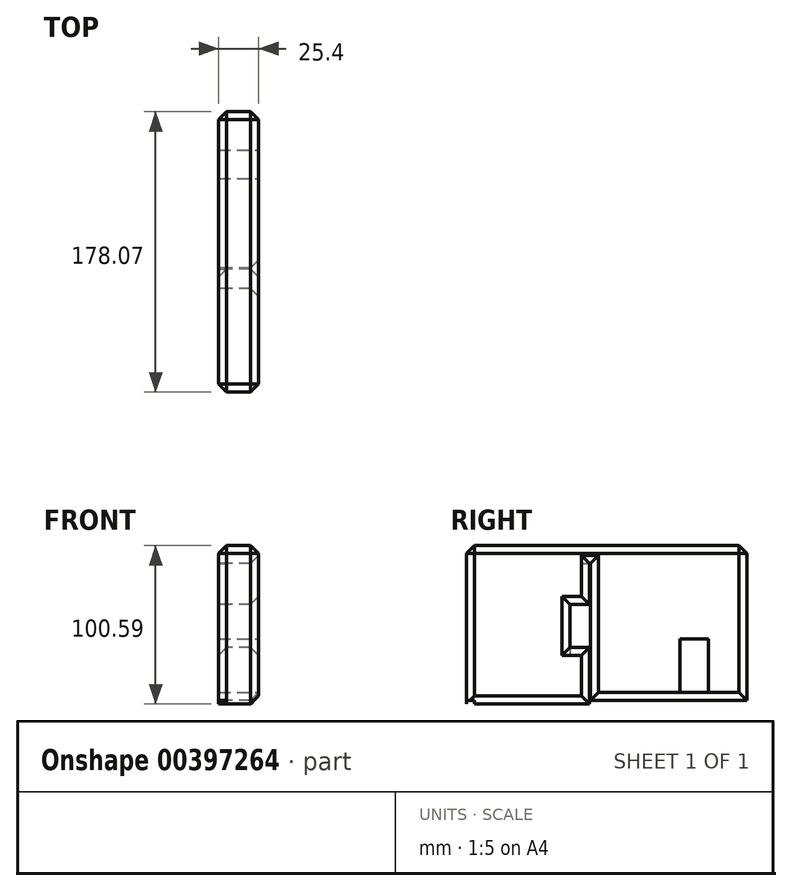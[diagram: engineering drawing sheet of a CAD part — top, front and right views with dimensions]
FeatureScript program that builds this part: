
annotation { "Feature Type Name" : "Feature", "Feature Type Description" : "" }
export const myFeature = defineFeature(function(context is Context, id is Id, definition is map)
    precondition{}
    {
        {
            var Q0;
            Q0=qCreatedBy(makeId("Right.planeOp"),FACE);
            var sketch = newSketch(context, id + "F0", { "sketchPlane" : qUnion([Q0])});
            skLineSegment(sketch, "E0.bottom", {"start": v(-42.81, -11.37) * mm, "end": v(56.46, -11.37) * mm});
            skLineSegment(sketch, "E0.top", {"start": v(-42.81, 42.16) * mm, "end": v(56.46, 42.16) * mm});
            skLineSegment(sketch, "E0.left", {"start": v(-42.81, -11.37) * mm, "end": v(-42.81, 42.16) * mm});
            skLineSegment(sketch, "E0.right", {"start": v(56.46, -11.37) * mm, "end": v(56.46, 42.16) * mm});
            skLineSegment(sketch, "E1.bottom", {"start": v(-55.84, 15.92) * mm, "end": v(-121.61, 15.92) * mm});
            skLineSegment(sketch, "E1.top", {"start": v(-55.84, -10.3) * mm, "end": v(-121.61, -10.3) * mm});
            skLineSegment(sketch, "E1.left", {"start": v(-55.84, 15.92) * mm, "end": v(-55.84, -10.3) * mm});
            skLineSegment(sketch, "E1.right", {"start": v(-121.61, 15.92) * mm, "end": v(-121.61, -10.3) * mm});
            skLineSegment(sketch, "E2.bottom", {"start": v(-121.61, 15.92) * mm, "end": v(-43.43, 15.92) * mm});
            skLineSegment(sketch, "E2.top", {"start": v(-121.61, 53.42) * mm, "end": v(-43.43, 53.42) * mm});
            skLineSegment(sketch, "E2.left", {"start": v(-121.61, 15.92) * mm, "end": v(-121.61, 53.42) * mm});
            skLineSegment(sketch, "E2.right", {"start": v(-43.43, 15.92) * mm, "end": v(-43.43, 53.42) * mm});
            skLineSegment(sketch, "E3.bottom", {"start": v(-55.84, -10.3) * mm, "end": v(-42.81, -10.3) * mm});
            skLineSegment(sketch, "E3.top", {"start": v(-55.84, -11.37) * mm, "end": v(-42.81, -11.37) * mm});
            skLineSegment(sketch, "E3.left", {"start": v(-55.84, -10.3) * mm, "end": v(-55.84, -11.37) * mm});
            skLineSegment(sketch, "E3.right", {"start": v(-42.81, -10.3) * mm, "end": v(-42.81, -11.37) * mm});
            skLineSegment(sketch, "E4.bottom", {"start": v(-42.81, -10.3) * mm, "end": v(-55.84, -10.3) * mm});
            skLineSegment(sketch, "E4.top", {"start": v(-42.81, 15.92) * mm, "end": v(-55.84, 15.92) * mm});
            skLineSegment(sketch, "E4.left", {"start": v(-42.81, -10.3) * mm, "end": v(-42.81, 15.92) * mm});
            skLineSegment(sketch, "E4.right", {"start": v(-55.84, -10.3) * mm, "end": v(-55.84, 15.92) * mm});
            skLineSegment(sketch, "E5.bottom", {"start": v(-43.43, 53.42) * mm, "end": v(56.46, 53.42) * mm});
            skLineSegment(sketch, "E5.top", {"start": v(-43.43, 42.16) * mm, "end": v(56.46, 42.16) * mm});
            skLineSegment(sketch, "E5.left", {"start": v(-43.43, 53.42) * mm, "end": v(-43.43, 42.16) * mm});
            skLineSegment(sketch, "E5.right", {"start": v(56.46, 53.42) * mm, "end": v(56.46, 42.16) * mm});
            skLineSegment(sketch, "E6.top", {"start": v(-42.81, -45.03) * mm, "end": v(56.46, -45.03) * mm});
            skLineSegment(sketch, "E6.left", {"start": v(-42.81, -11.37) * mm, "end": v(-42.81, -45.03) * mm});
            skLineSegment(sketch, "E6.right", {"start": v(56.46, -11.37) * mm, "end": v(56.46, -45.03) * mm});
            skLineSegment(sketch, "E7.bottom", {"start": v(-121.61, -10.3) * mm, "end": v(-43.43, -10.3) * mm});
            skLineSegment(sketch, "E7.top", {"start": v(-121.61, -47.17) * mm, "end": v(-43.43, -47.17) * mm});
            skLineSegment(sketch, "E7.left", {"start": v(-121.61, -10.3) * mm, "end": v(-121.61, -47.17) * mm});
            skLineSegment(sketch, "E7.right", {"start": v(-43.43, -10.3) * mm, "end": v(-43.43, -47.17) * mm});
            skSolve(sketch);
        }
        {
            var Q0;
            {var subQ1=sQuery(id+"F0.wireOp",EDGE,"E2.bottom");Q0=makeQuery(id+"F0.imprint","IMPRINT",FACE,{"disambiguationData":[TD([[makeQuery(id+"F0.imprint","IMPRINT",EDGE,{"derivedFrom":subQ1}),1.0]])]});}
            var Q1;
            {var subQ0=sQuery(id+"F0.wireOp",EDGE,"E1.right");Q1=makeQuery(id+"F0.imprint","IMPRINT",FACE,{"disambiguationData":[TD([[makeQuery(id+"F0.imprint","IMPRINT",EDGE,{"derivedFrom":subQ0}),1.0]])]});}
            var Q2;
            {var subQ4=sQuery(id+"F0.wireOp",EDGE,"E4.bottom");Q2=makeQuery(id+"F0.imprint","IMPRINT",FACE,{"disambiguationData":[TD([[makeQuery(id+"F0.imprint","IMPRINT",EDGE,{"derivedFrom":subQ4}),-1.0]])]});}
            var Q3;
            {var subQ2=sQuery(id+"F0.wireOp",EDGE,"E3.left");Q3=makeQuery(id+"F0.imprint","IMPRINT",FACE,{"disambiguationData":[TD([[makeQuery(id+"F0.imprint","IMPRINT",EDGE,{"derivedFrom":subQ2}),-1.0]])]});}
            var Q4;
            Q4=makeQuery(id+"F0.imprint","IMPRINT",FACE,{"disambiguationData":[TD([[makeQuery(id+"F0.imprint","IMPRINT",EDGE,{"derivedFrom":sQuery(id+"F0.wireOp",EDGE,"E0.bottom")}),-1.0]])]});
            var Q5;
            {var subQ1=sQuery(id+"F0.wireOp",EDGE,"E0.left");Q5=makeQuery(id+"F0.imprint","IMPRINT",FACE,{"disambiguationData":[TD([[makeQuery(id+"F0.imprint","IMPRINT",EDGE,{"derivedFrom":subQ1}),-1.0]])]});}
            var Q6;
            Q6=makeQuery(id+"F0.imprint","IMPRINT",FACE,{"disambiguationData":[TD([[makeQuery(id+"F0.imprint","IMPRINT",EDGE,{"derivedFrom":sQuery(id+"F0.wireOp",EDGE,"E5.bottom")}),-1.0]])]});
            extrude(context, id + "F1", {"entities" : qUnion([Q0, Q1, Q2, Q3, Q4, Q5, Q6]), "depth" : 25.4 * mm});
        }
        {
            var Q0;
            Q0=makeQuery(id+"F1.opExtrude","CAP_EDGE",EDGE,{"disambiguationData":[OSD([sQuery(id+"F0.wireOp",EDGE,"E2.top"),sQuery(id+"F0.wireOp",EDGE,"E5.bottom")])],"isStart":true});
            var Q1;
            Q1=makeQuery(id+"F1.opExtrude","SWEPT_FACE",FACE,{"disambiguationData":[OSD([sQuery(id+"F0.wireOp",EDGE,"E2.top"),sQuery(id+"F0.wireOp",EDGE,"E5.bottom")])]});
            var Q2;
            Q2=makeQuery(id+"F1.opExtrude","CAP_EDGE",EDGE,{"disambiguationData":[OSD([sQuery(id+"F0.wireOp",EDGE,"E1.right"),sQuery(id+"F0.wireOp",EDGE,"E2.left"),sQuery(id+"F0.wireOp",EDGE,"E7.left")])],"isStart":false});
            var Q3;
            Q3=makeQuery(id+"F1.opExtrude","CAP_EDGE",EDGE,{"disambiguationData":[OSD([sQuery(id+"F0.wireOp",EDGE,"E1.right"),sQuery(id+"F0.wireOp",EDGE,"E2.left"),sQuery(id+"F0.wireOp",EDGE,"E7.left")])],"isStart":true});
            var Q4;
            Q4=makeQuery(id+"F1.opExtrude","CAP_EDGE",EDGE,{"disambiguationData":[OSD([sQuery(id+"F0.wireOp",EDGE,"E0.right"),sQuery(id+"F0.wireOp",EDGE,"E5.right"),sQuery(id+"F0.wireOp",EDGE,"E6.right")])],"isStart":false});
            var Q5;
            Q5=makeQuery(id+"F1.opExtrude","CAP_EDGE",EDGE,{"disambiguationData":[OSD([sQuery(id+"F0.wireOp",EDGE,"E0.left")])],"isStart":false});
            var Q6;
            Q6=makeQuery(id+"F1.opExtrude","CAP_EDGE",EDGE,{"disambiguationData":[OSD([sQuery(id+"F0.wireOp",EDGE,"E3.top")])],"isStart":false});
            var Q7;
            Q7=makeQuery(id+"F1.opExtrude","CAP_FACE",FACE,{"disambiguationData":[OSD([sQuery(id+"F0.wireOp",EDGE,"E0.left"),sQuery(id+"F0.wireOp",EDGE,"E0.right"),sQuery(id+"F0.wireOp",EDGE,"E1.right"),sQuery(id+"F0.wireOp",EDGE,"E2.top"),sQuery(id+"F0.wireOp",EDGE,"E2.left"),sQuery(id+"F0.wireOp",EDGE,"E2.right"),sQuery(id+"F0.wireOp",EDGE,"E3.top"),sQuery(id+"F0.wireOp",EDGE,"E3.left"),sQuery(id+"F0.wireOp",EDGE,"E3.right"),sQuery(id+"F0.wireOp",EDGE,"E4.bottom"),sQuery(id+"F0.wireOp",EDGE,"E4.top"),sQuery(id+"F0.wireOp",EDGE,"E5.bottom"),sQuery(id+"F0.wireOp",EDGE,"E5.top"),sQuery(id+"F0.wireOp",EDGE,"E5.right"),sQuery(id+"F0.wireOp",EDGE,"E6.top"),sQuery(id+"F0.wireOp",EDGE,"E6.left"),sQuery(id+"F0.wireOp",EDGE,"E6.right"),sQuery(id+"F0.wireOp",EDGE,"E7.bottom"),sQuery(id+"F0.wireOp",EDGE,"E7.top"),sQuery(id+"F0.wireOp",EDGE,"E7.left"),sQuery(id+"F0.wireOp",EDGE,"E7.right")])],"isStart":false});
            var Q8;
            Q8=makeQuery(id+"F1.opExtrude","CAP_EDGE",EDGE,{"disambiguationData":[OSD([sQuery(id+"F0.wireOp",EDGE,"E2.right")])],"isStart":true});
            var Q9;
            Q9=makeQuery(id+"F1.opExtrude","CAP_EDGE",EDGE,{"disambiguationData":[OSD([sQuery(id+"F0.wireOp",EDGE,"E3.top")])],"isStart":true});
            var Q10;
            Q10=makeQuery(id+"F1.opExtrude","CAP_EDGE",EDGE,{"disambiguationData":[OSD([sQuery(id+"F0.wireOp",EDGE,"E0.right"),sQuery(id+"F0.wireOp",EDGE,"E5.right"),sQuery(id+"F0.wireOp",EDGE,"E6.right")])],"isStart":true});
            chamfer(context, id + "F2", {"entities" : qUnion([Q0, Q1, Q2, Q3, Q4, Q5, Q6, Q7, Q8, Q9, Q10]), "width" : 5.08 * mm, "tangentPropagation" : true});
        }
        {
            var Q0;
            Q0=makeQuery(id+"F1.opExtrude","CAP_FACE",FACE,{"disambiguationData":[OSD([sQuery(id+"F0.wireOp",EDGE,"E0.left"),sQuery(id+"F0.wireOp",EDGE,"E0.right"),sQuery(id+"F0.wireOp",EDGE,"E1.right"),sQuery(id+"F0.wireOp",EDGE,"E2.top"),sQuery(id+"F0.wireOp",EDGE,"E2.left"),sQuery(id+"F0.wireOp",EDGE,"E2.right"),sQuery(id+"F0.wireOp",EDGE,"E3.top"),sQuery(id+"F0.wireOp",EDGE,"E3.left"),sQuery(id+"F0.wireOp",EDGE,"E3.right"),sQuery(id+"F0.wireOp",EDGE,"E4.bottom"),sQuery(id+"F0.wireOp",EDGE,"E4.top"),sQuery(id+"F0.wireOp",EDGE,"E5.bottom"),sQuery(id+"F0.wireOp",EDGE,"E5.top"),sQuery(id+"F0.wireOp",EDGE,"E5.right"),sQuery(id+"F0.wireOp",EDGE,"E6.top"),sQuery(id+"F0.wireOp",EDGE,"E6.left"),sQuery(id+"F0.wireOp",EDGE,"E6.right"),sQuery(id+"F0.wireOp",EDGE,"E7.bottom"),sQuery(id+"F0.wireOp",EDGE,"E7.top"),sQuery(id+"F0.wireOp",EDGE,"E7.left"),sQuery(id+"F0.wireOp",EDGE,"E7.right")])],"isStart":false});
            var sketch = newSketch(context, id + "F3", { "sketchPlane" : qUnion([Q0])});
            skLineSegment(sketch, "E8.bottom", {"start": v(13.98, -39.95) * mm, "end": v(32.1, -39.95) * mm});
            skLineSegment(sketch, "E8.top", {"start": v(13.98, -5.98) * mm, "end": v(32.1, -5.98) * mm});
            skLineSegment(sketch, "E8.left", {"start": v(13.98, -39.95) * mm, "end": v(13.98, -5.98) * mm});
            skLineSegment(sketch, "E8.right", {"start": v(32.1, -39.95) * mm, "end": v(32.1, -5.98) * mm});
            skSolve(sketch);
        }
        {
            var Q0;
            Q0=makeQuery(id+"F3.imprint","IMPRINT",FACE,{"disambiguationData":[TD([[makeQuery(id+"F3.imprint","IMPRINT",EDGE,{"derivedFrom":sQuery(id+"F3.wireOp",EDGE,"E8.top")}),1.0]])]});
            var sketch = newSketch(context, id + "F4", { "sketchPlane" : qUnion([Q0])});
            skLineSegment(sketch, "E9.bottom", {"start": v(15.2, -6.84) * mm, "end": v(31.17, -6.84) * mm});
            skLineSegment(sketch, "E9.top", {"start": v(15.2, -39.28) * mm, "end": v(31.17, -39.28) * mm});
            skLineSegment(sketch, "E9.left", {"start": v(15.2, -6.84) * mm, "end": v(15.2, -39.28) * mm});
            skLineSegment(sketch, "E9.right", {"start": v(31.17, -6.84) * mm, "end": v(31.17, -39.28) * mm});
            skSolve(sketch);
        }
        {
            var Q0;
            Q0=makeQuery(id+"F4.imprint","IMPRINT",FACE,{"disambiguationData":[TD([[makeQuery(id+"F4.imprint","IMPRINT",EDGE,{"derivedFrom":sQuery(id+"F4.wireOp",EDGE,"E9.bottom")}),-1.0]])]});
            var Q1;
            Q1=makeQuery(id+"F1.opExtrude","SWEPT_BODY",BODY,{"disambiguationData":[OSD([sQuery(id+"F0.wireOp",EDGE,"E0.left"),sQuery(id+"F0.wireOp",EDGE,"E0.right"),sQuery(id+"F0.wireOp",EDGE,"E1.right"),sQuery(id+"F0.wireOp",EDGE,"E2.top"),sQuery(id+"F0.wireOp",EDGE,"E2.left"),sQuery(id+"F0.wireOp",EDGE,"E2.right"),sQuery(id+"F0.wireOp",EDGE,"E3.top"),sQuery(id+"F0.wireOp",EDGE,"E3.left"),sQuery(id+"F0.wireOp",EDGE,"E3.right"),sQuery(id+"F0.wireOp",EDGE,"E4.bottom"),sQuery(id+"F0.wireOp",EDGE,"E4.top"),sQuery(id+"F0.wireOp",EDGE,"E5.bottom"),sQuery(id+"F0.wireOp",EDGE,"E5.top"),sQuery(id+"F0.wireOp",EDGE,"E5.right"),sQuery(id+"F0.wireOp",EDGE,"E6.top"),sQuery(id+"F0.wireOp",EDGE,"E6.left"),sQuery(id+"F0.wireOp",EDGE,"E6.right"),sQuery(id+"F0.wireOp",EDGE,"E7.bottom"),sQuery(id+"F0.wireOp",EDGE,"E7.top"),sQuery(id+"F0.wireOp",EDGE,"E7.left"),sQuery(id+"F0.wireOp",EDGE,"E7.right")])]});
            extrude(context, id + "F5", {"entities" : qUnion([Q0]), "operationType" : NewBodyOperationType.ADD, "endBound" : BoundingType.UP_TO_BODY, "oppositeDirection" : true, "endBoundEntityBody" : qUnion([Q1]), "depth" : 25.4 * mm});
        }
        {
            var Q0;
            Q0=makeQuery(id+"F3.imprint","IMPRINT",FACE,{"disambiguationData":[TD([[makeQuery(id+"F3.imprint","IMPRINT",EDGE,{"derivedFrom":sQuery(id+"F3.wireOp",EDGE,"E8.bottom")}),1.0]])]});
            extrude(context, id + "F6", {"entities" : qUnion([Q0]), "operationType" : NewBodyOperationType.REMOVE, "endBound" : BoundingType.THROUGH_ALL, "oppositeDirection" : true, "depth" : 25.4 * mm});
        }
        {
            var Q0;
            Q0=makeQuery(id+"F1.opExtrude","CAP_FACE",FACE,{"disambiguationData":[OSD([sQuery(id+"F0.wireOp",EDGE,"E0.left"),sQuery(id+"F0.wireOp",EDGE,"E0.right"),sQuery(id+"F0.wireOp",EDGE,"E1.right"),sQuery(id+"F0.wireOp",EDGE,"E2.top"),sQuery(id+"F0.wireOp",EDGE,"E2.left"),sQuery(id+"F0.wireOp",EDGE,"E2.right"),sQuery(id+"F0.wireOp",EDGE,"E3.top"),sQuery(id+"F0.wireOp",EDGE,"E3.left"),sQuery(id+"F0.wireOp",EDGE,"E3.right"),sQuery(id+"F0.wireOp",EDGE,"E4.bottom"),sQuery(id+"F0.wireOp",EDGE,"E4.top"),sQuery(id+"F0.wireOp",EDGE,"E5.bottom"),sQuery(id+"F0.wireOp",EDGE,"E5.top"),sQuery(id+"F0.wireOp",EDGE,"E5.right"),sQuery(id+"F0.wireOp",EDGE,"E6.top"),sQuery(id+"F0.wireOp",EDGE,"E6.left"),sQuery(id+"F0.wireOp",EDGE,"E6.right"),sQuery(id+"F0.wireOp",EDGE,"E7.bottom"),sQuery(id+"F0.wireOp",EDGE,"E7.top"),sQuery(id+"F0.wireOp",EDGE,"E7.left"),sQuery(id+"F0.wireOp",EDGE,"E7.right")])],"isStart":true});
            var sketch = newSketch(context, id + "F7", { "sketchPlane" : qUnion([Q0])});
            skLineSegment(sketch, "E10.bottom", {"start": v(-51.38, -45.03) * mm, "end": v(121.52, -45.03) * mm});
            skLineSegment(sketch, "E10.top", {"start": v(-51.38, -72.26) * mm, "end": v(121.52, -72.26) * mm});
            skLineSegment(sketch, "E10.left", {"start": v(-51.38, -45.03) * mm, "end": v(-51.38, -72.26) * mm});
            skLineSegment(sketch, "E10.right", {"start": v(121.52, -45.03) * mm, "end": v(121.52, -72.26) * mm});
            skSolve(sketch);
        }
        {
            var Q0;
            Q0=makeQuery(id+"F7.imprint","IMPRINT",FACE,{"disambiguationData":[TD([[makeQuery(id+"F7.imprint","IMPRINT",EDGE,{"derivedFrom":sQuery(id+"F7.wireOp",EDGE,"E10.top")}),1.0]])]});
            extrude(context, id + "F8", {"entities" : qUnion([Q0]), "operationType" : NewBodyOperationType.REMOVE, "endBound" : BoundingType.THROUGH_ALL, "oppositeDirection" : true, "depth" : 25.4 * mm});
        }
    });
